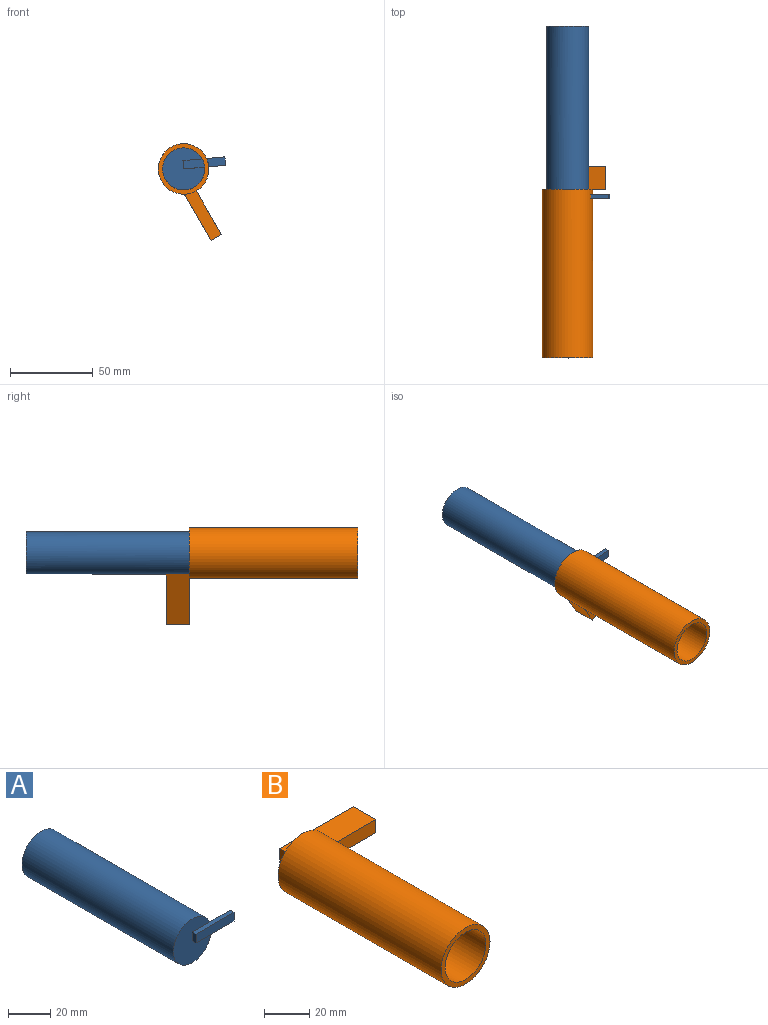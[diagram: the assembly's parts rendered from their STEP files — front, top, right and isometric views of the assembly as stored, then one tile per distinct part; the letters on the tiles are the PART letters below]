
ASSEMBLY  parts=2 mates=1
PART A: 9 faces, bbox 38.1x104.1x25.4 mm
  f0: plane 25.4x25.4mm, normal (0,-1,0), area 444mm2, adj f1,f4,f5,f6
  f1: cylinder r=12.7mm len=101.6mm, axis (0,1,0), area 8107.3mm2, adj f0,f2,f3
  f2: plane 25.4x25.4mm, normal (0,1,0), area 506.7mm2, adj f1
  f3: plane 13.76x5.08mm, normal (0,1,0), area 66.3mm2, adj f1,f4,f6,f7
  f4: plane 25.4x2.54mm, normal (0,0,1), area 64.5mm2, adj f0,f3,f5,f7,f8
  f5: plane 5.08x2.54mm, normal (-1,0,0), area 12.9mm2, adj f0,f4,f6,f8
  f6: plane 25.4x2.54mm, normal (0,0,-1), area 64.5mm2, adj f0,f3,f5,f7,f8
  f7: plane 5.08x2.54mm, normal (1,0,0), area 12.9mm2, adj f3,f4,f6,f8
  f8: plane 25.4x5.08mm, normal (0,-1,0), area 129mm2, adj f4,f5,f6,f7
PART B: 11 faces, bbox 60.8x115.6x30.5 mm
  f0: cylinder r=15.24mm len=101.6mm, axis (0,1,0), area 9728.8mm2, adj f1,f2,f9
  f1: plane 30.48x30.48mm, normal (0,-1,0), area 223mm2, adj f0,f3
  f2: plane 30.48x30.48mm, normal (0,1,0), area 624.7mm2, adj f0,f5,f6,f7
  f3: cylinder r=12.7mm len=99.06mm, axis (0,1,0), area 7904.6mm2, adj f1,f4
  f4: plane 25.4x25.4mm, normal (0,-1,0), area 506.7mm2, adj f3
  f5: plane 45.53x14mm, normal (0,0,-1), area 637.3mm2, adj f2,f6,f8,f9,f10
  f6: plane 14x7.16mm, normal (-1,0,0), area 100.2mm2, adj f2,f5,f7,f10
  f7: plane 45.53x14mm, normal (0,0,1), area 637.3mm2, adj f2,f6,f8,f9,f10
  f8: plane 14x7.16mm, normal (1,0,0), area 100.2mm2, adj f5,f7,f9,f10
  f9: plane 32.08x7.16mm, normal (0,-1,0), area 221.1mm2, adj f0,f5,f7,f8
  f10: plane 45.53x7.16mm, normal (0,1,0), area 326.1mm2, adj f5,f6,f7,f8
PLACE A rot(axis=(0,-1,0),5deg) t=(-26.25,25.52,-12.19)mm
PLACE B rot(axis=(0,1,0),60deg) t=(-26.25,-72.99,-12.19)mm
MATE cylindrical B.f0 <-> A.f1  axis (0,-1,0) through (-26.25,-75.53,-12.19)mm
